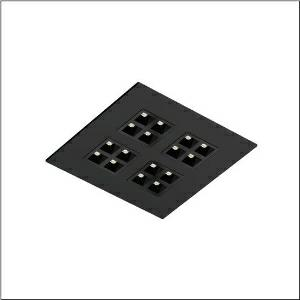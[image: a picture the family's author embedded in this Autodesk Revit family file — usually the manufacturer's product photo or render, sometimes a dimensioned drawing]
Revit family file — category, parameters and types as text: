
# Revit family: silica_r__31_square_51my6lmu34ba_84fe
name_source: partatom
category: Lighting Fixtures
units: mm (PartAtom-declared; Revit-internal decimal feet)

## family parameters
Cut with Voids When Loaded = No
Host = Face
Light Source = No
Part Type = Normal
Room Calculation Point = No
Round Connector Dimension = Use Diameter
Shared = No

## types (1)
- --- (1 x LED, 6250 lm, 39 W, 3000K)
    Apparent Load = 39 VA
    CIE Flux Codes = 82 100 100 100 100
    Color Rendering = 80
    Color Temperature = 3000K
    Default Elevation = 1800 mm
    Description = Silica® 31 Square, office luminaire, primary light control with lens, of PMMA, primary anti-glare with reflector, of PC, black, light emission: direct distribution, primary light characteristic: symmetric, installation type: lay-in mounting, LED, rated luminous flux: 4.600lm, luminous efficacy: 166lm/W, light colour: 830, colour temperature: 3000K, control gear: ON/OFF Multilumen, with terminal, 3-pole, mains connection: 220..240V, AC, 50/60Hz, rated input power: 27.7W, luminaire housing, of sheet steel, coated, jet black (RAL 9005), module: M625, length: 620mm, width: 620mm, height: 43mm, protection rating (complete): IP20, insulation class (complete): insulation class II (safety insulation), certification: CE, impact resistance: IK03, permissible operating ambient temperature: -20..+35°C, standard: EN 50419, packaging unit: 1 piece
    Height = 0 mm  [stored 0 ft]
    Lamp = 1 x LED
    Lamp Light Flux = 6250 lm
    Lamp Power = 39 W
    Lamp count = 1
    Length = 620 mm
    Luminous efficacy = 160 lm/W
    Manufacturer = Siteco
    ModVariant = No
    Model = 51MY6LMU34BA
    Mounting Place = Ceiling
    Mounting Type = Recessed
    Number of Poles = 1
    OnlyDefault = Yes
    Power Factor = 1
    Product Name = Silica® 31 Square
    Product group = office luminaire | ceiling recessed
    ProductGroupID = 401
    Protection Class = Protection class II
    Protection Degree = IP 20
    RLX_Detail_Level = 1
    RLX_Emergency_Light_Flux = 0 lm
    RLX_Emergency_Type = 0
    RLX_Emergency_Type_DB = No
    RlxData = <blob elided: 36337 chars, md5=939b2a71>
    Socket = socket
    Standby Power = 0 W
    System Light Flux = 6250 lm
    System Power = 39 W
    Type Comments = factory setting: luminous flux: 100 % | (ON | ON | ON | ON) | 1100 mA
    Type Image = l_1313660.jpg
    URL = http://relux.com
    VarID = @adj_036250
    Voltage = 0 V
    Weight = 0.00 kg
    Width = 620 mm

note: [stored X ft] marks values corroborated as IEEE doubles in the binary element streams (Revit-internal decimal feet)

## geometry (parser evidence)
native form markers: Blend x4, Sweep x11
no freeform markers — native parametric forms only
